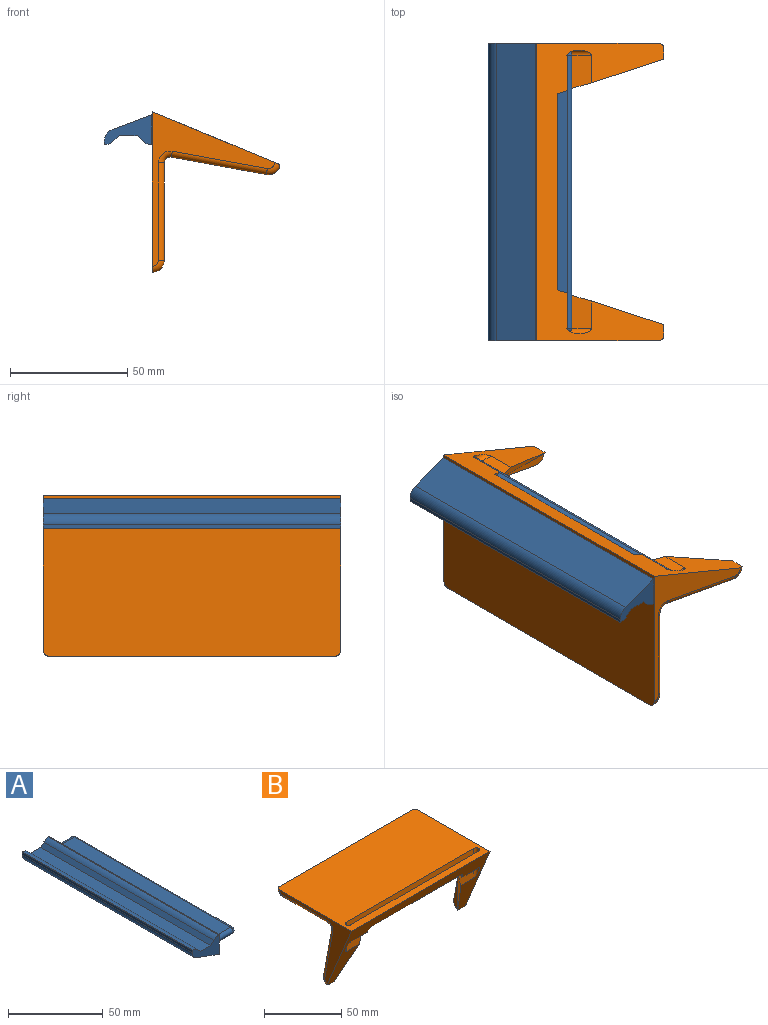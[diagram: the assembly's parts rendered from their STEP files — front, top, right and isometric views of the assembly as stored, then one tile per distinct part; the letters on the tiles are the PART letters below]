
ASSEMBLY  parts=2 mates=1
PART A: 22 faces, bbox 35.6x127x12.7 mm
  f0: plane 127x0.44mm, normal (0,0,1), area 55.3mm2, adj f1,f11,f13,f20
  f1: plane 20.32x12.7mm, normal (0,-1,0), area 133.7mm2, adj f0,f11,f12,f14,f15,f16,f17,f18
  f2: plane 116.84x13.46mm, normal (0,0,-1), area 1572.9mm2, adj f3,f5,f9,f11
  f3: cylinder r=1.91mm len=13.46mm, axis (-1,0,0), area 80.6mm2, adj f2,f4,f7,f11
  f4: plane 116.84x13.46mm, normal (0,0,1), area 1572.9mm2, adj f3,f5,f8,f11
  f5: cylinder r=1.91mm len=13.46mm, axis (-1,0,0), area 80.6mm2, adj f2,f4,f10,f11
  f6: plane 117.09x0.25mm, normal (1,0,0), area 29.7mm2, adj f7,f8,f9,f10
  f7: torus R=0.13mm, axis (1,0,0), area 11mm2, adj f3,f6,f8,f9
  f8: cylinder r=1.78mm len=116.84mm, axis (0,1,0), area 326.3mm2, adj f4,f6,f7,f10
  f9: cylinder r=1.78mm len=116.84mm, axis (0,-1,0), area 326.3mm2, adj f2,f6,f7,f10
  f10: torus R=0.13mm, axis (1,0,0), area 11mm2, adj f5,f6,f8,f9
  f11: plane 127x12.7mm, normal (1,0,0), area 1156.3mm2, adj f0,f1,f2,f3,f4,f5,f13,f16
  f12: plane 127x0.44mm, normal (0,0,1), area 55.3mm2, adj f1,f13,f14,f21
  f13: plane 20.32x12.7mm, normal (0,1,0), area 133.7mm2, adj f0,f11,f12,f14,f15,f16,f17,f18
  f14: plane 127x1.56mm, normal (-1,0,0), area 198.1mm2, adj f1,f12,f13,f19
  f15: plane 127x7.62mm, normal (0,0,1), area 967.7mm2, adj f1,f13,f17,f18
  f16: plane 127x17.02mm, normal (-0.35,0,-0.94), area 2309mm2, adj f1,f11,f13,f19
  f17: plane 127x2.32mm, normal (-0.71,0,0.71), area 417.1mm2, adj f1,f13,f15,f20
  f18: plane 127x2.32mm, normal (0.71,0,0.71), area 417.1mm2, adj f1,f13,f15,f21
  f19: cylinder r=5.08mm len=127mm, axis (0,1,0), area 782mm2, adj f1,f13,f14,f16
  f20: cylinder r=5.08mm len=127mm, axis (0,-1,0), area 506.7mm2, adj f0,f1,f13,f17
  f21: cylinder r=5.08mm len=127mm, axis (0,1,0), area 506.7mm2, adj f1,f12,f13,f18
PART B: 44 faces, bbox 127x69x55.1 mm
  f0: plane 4.28x3.65mm, normal (1,0,0), area 3.4mm2, adj f13,f26,f28,f30
  f1: plane 31.17x4.77mm, normal (-1,0,0), area 67.2mm2, adj f9,f24,f25,f31
  f2: plane 66.04x52.14mm, normal (-1,0,0), area 617mm2, adj f7,f12,f34,f35,f36,f37,f38
  f3: plane 66.04x52.14mm, normal (1,0,0), area 617mm2, adj f7,f12,f39,f40,f41,f42,f43
  f4: plane 31.17x4.77mm, normal (1,0,0), area 67.2mm2, adj f8,f23,f26,f32
  f5: plane 4.28x3.65mm, normal (-1,0,0), area 3.4mm2, adj f13,f25,f27,f29
  f6: plane 1.15x0.37mm, normal (0,0.95,0.31), area 0.2mm2, adj f13,f23,f28
  f7: plane 127x54.37mm, normal (0,-0.92,-0.38), area 2306.7mm2, adj f2,f3,f8,f9,f10,f11,f12,f14
  f8: plane 5.4x1.54mm, normal (0,0.14,-0.99), area 7.5mm2, adj f4,f7,f21,f23,f32,f38
  f9: plane 5.4x1.54mm, normal (0,0.14,-0.99), area 7.5mm2, adj f1,f7,f22,f24,f31,f43
  f10: plane 116.84x23.46mm, normal (0,-1,0), area 1279.7mm2, adj f7,f12,f14,f15,f20,f21,f22,f23
  f11: plane 116.84x13.34mm, normal (0,1,0), area 1145.5mm2, adj f7,f12,f14,f15,f17,f18,f19
  f12: plane 127x68.58mm, normal (0,0,1), area 8203.4mm2, adj f2,f3,f7,f10,f11,f14,f15,f33
  f13: plane 121.92x47.43mm, normal (0,0,-1), area 5726.1mm2, adj f0,f5,f6,f16,f20,f27,f28,f29
  f14: cylinder r=2.1mm len=23.46mm, axis (0,0,1), area 121.1mm2, adj f7,f10,f11,f12
  f15: cylinder r=2.1mm len=23.46mm, axis (0,0,1), area 121.1mm2, adj f7,f10,f11,f12
  f16: plane 1.15x0.37mm, normal (0,0.95,0.31), area 0.2mm2, adj f13,f24,f27
  f17: plane 4.84x1.77mm, normal (-0.96,0.09,-0.28), area 4.5mm2, adj f7,f11,f18
  f18: plane 83.82x1.77mm, normal (0,0.31,-0.95), area 155.9mm2, adj f7,f11,f17,f19
  f19: plane 4.84x1.77mm, normal (0.96,0.09,-0.28), area 4.5mm2, adj f7,f11,f18
  f20: plane 102.39x6.36mm, normal (0,0.31,-0.95), area 637.6mm2, adj f10,f13,f23,f24
  f21: plane 40.06x12.95mm, normal (0.96,0.09,-0.28), area 64.4mm2, adj f7,f8,f10,f23
  f22: plane 40.06x12.95mm, normal (-0.96,0.09,-0.28), area 64.4mm2, adj f7,f9,f10,f24
  f23: plane 49.27x13.38mm, normal (0.68,0.74,0.02), area 470mm2, adj f4,f6,f8,f10,f20,f21,f26,f28
  f24: plane 49.27x13.38mm, normal (-0.68,0.74,0.02), area 470mm2, adj f1,f9,f10,f16,f20,f22,f25,f27
  f25: plane 40.61x7.44mm, normal (0,0.98,0.18), area 168.2mm2, adj f1,f5,f24,f27,f29,f31,f42
  f26: plane 40.61x7.44mm, normal (0,0.98,0.18), area 168.2mm2, adj f0,f4,f23,f28,f30,f32,f37
  f27: plane 8.56x5.59mm, normal (-0.34,0.89,0.29), area 33.1mm2, adj f5,f13,f16,f24,f25
  f28: plane 8.56x5.59mm, normal (0.34,0.89,0.29), area 33.1mm2, adj f0,f6,f13,f23,f26
  f29: cylinder r=2.54mm len=3.81mm, axis (1,0,0), area 17mm2, adj f5,f13,f25,f41
  f30: cylinder r=2.54mm len=3.81mm, axis (1,0,0), area 17mm2, adj f0,f13,f26,f36
  f31: cylinder r=5.08mm len=5.47mm, axis (-1,0,0), area 25mm2, adj f1,f9,f25,f43
  f32: cylinder r=5.08mm len=5.47mm, axis (-1,0,0), area 25mm2, adj f4,f8,f26,f38
  f33: cylinder r=5.08mm len=121.92mm, axis (-1,0,0), area 972.9mm2, adj f12,f13,f34,f39
  f34: torus R=2.54mm, axis (1,0,0), area 26.1mm2, adj f2,f12,f33,f35
  f35: cylinder r=2.54mm len=41.64mm, axis (0,1,0), area 166.1mm2, adj f2,f13,f34,f36
  f36: torus R=5.08mm, axis (1,0,0), area 24.2mm2, adj f2,f30,f35,f37
  f37: cylinder r=2.54mm len=41.06mm, axis (0,0.18,-0.98), area 164.7mm2, adj f2,f26,f36,f38
  f38: torus R=2.54mm, axis (1,0,0), area 25.9mm2, adj f2,f7,f8,f32,f37
  f39: torus R=2.54mm, axis (1,0,0), area 26.1mm2, adj f3,f12,f33,f40
  f40: cylinder r=2.54mm len=41.64mm, axis (0,-1,0), area 166.1mm2, adj f3,f13,f39,f41
  f41: torus R=5.08mm, axis (1,0,0), area 24.2mm2, adj f3,f29,f40,f42
  f42: cylinder r=2.54mm len=41.06mm, axis (0,-0.18,0.98), area 164.7mm2, adj f3,f25,f41,f43
  f43: torus R=2.54mm, axis (1,0,0), area 25.9mm2, adj f3,f7,f9,f31,f42
PLACE A rot(axis=(1,0,0),180deg) t=(-29.3,8.22,108.56)mm
PLACE B rot(axis=(-0.58,-0.58,0.58),120deg) t=(-10.1,8.22,81.89)mm fixed
MATE slider A.f5 <-> B.f15  axis (1,0,0) through (-15.84,66.64,108.56)mm
